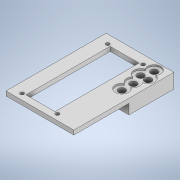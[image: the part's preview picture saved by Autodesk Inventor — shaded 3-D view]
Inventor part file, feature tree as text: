
AUTODESK INVENTOR PART (.ipt)
format: ipt  version: 2021 (Build 250183000, 183)  size: 212,480 bytes
history: native  units: in
note: dims shown in document units (in); Inventor stores cm internally (conversion verified against a paired STEP export)
features: extrude x5, sketch x5
ambient origin geometry x8: Origin, YZ Plane, XZ Plane, XY Plane, X Axis, Y Axis, Z Axis, Center Point
bodies: Solid1 (feature_tree)
feature tree (10):
  extrude  "Extrusion1"  Depth=1.0in
  extrude  "Extrusion3"  Depth=1.375in
  extrude  "Extrusion2"  Depth=2.335in
  extrude  "Extrusion5"  Depth=0.125in
  extrude  "Extrusion6"  Depth=0.2in
  sketch  "Sketch1"  dims[d0=2.9in d1=1.0in]
  sketch  "Sketch2"  dims[d4=3.35in d5=1.375in]
  sketch  "Sketch3"  dims[d6=2.335in d7=0.125in]
  sketch  "Sketch4"  dims[d8=0.125in d9=0.125in]
  sketch  "Sketch7"  dims[d10=0.125in d11=0.2in d12=0.35in d13=0.2in d14=0.765in d15=0.15in d16=0.0in d17=0.2375in d18=0.2375in d19=0.2375in d20=0.2375in d21=0.265in d22=0.405in d23=0.525in d24=0.2375in d25=0.175in d26=0.72in d27=0.35in d28=1.113in d29=0.0in d30=0.0in d31=1.45in d32=0.675in d33=0.35in d34=0.0in d35=0.45in d36=0.45in d37=0.45in d38=0.45in d39=0.45in d42=0.1in d43=0.0in d44=0.05in d45=0.0in]
